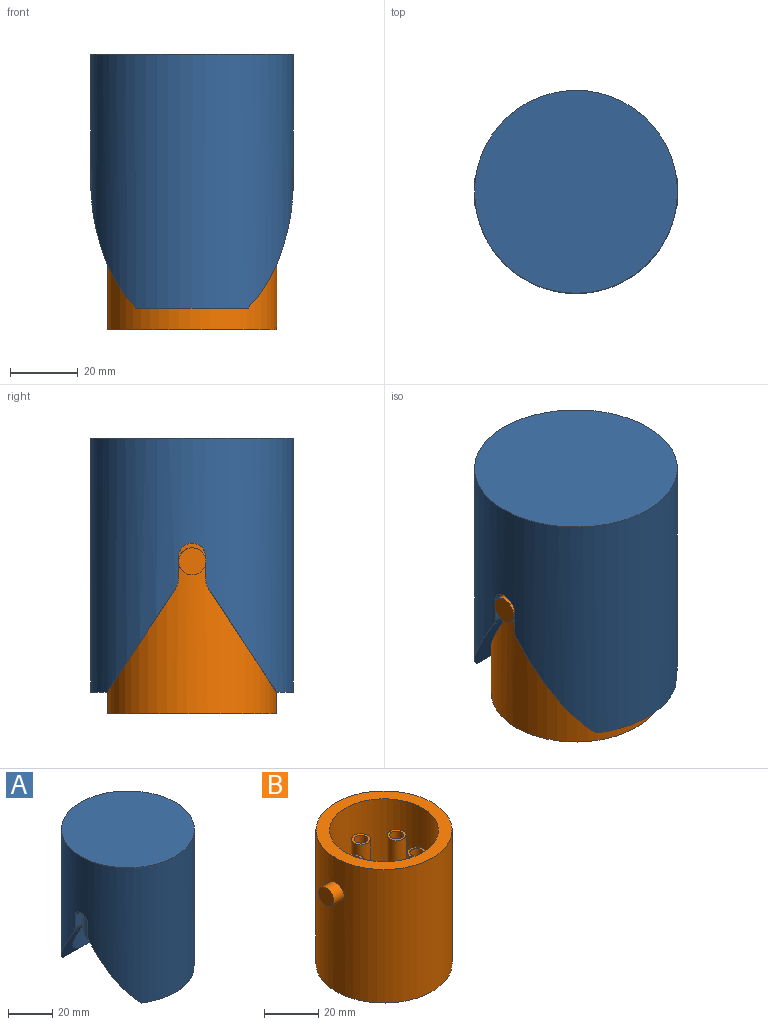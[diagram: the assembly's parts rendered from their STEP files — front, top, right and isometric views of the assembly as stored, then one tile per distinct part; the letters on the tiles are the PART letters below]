
ASSEMBLY  parts=2 mates=1
PART A: 42 faces, bbox 60x60x75 mm
  f0: cylinder r=25mm len=70mm, axis (0,0,1), area 8690.1mm2, adj f4,f28,f29,f30,f31,f32,f33,f34
  f1: cylinder r=30mm len=75mm, axis (0,0,-1), area 11956.4mm2, adj f2,f3,f27,f28,f29,f30,f31,f32
  f2: plane 33.17x5mm, normal (0,0,-1), area 112.5mm2, adj f1,f29,f36
  f3: plane 33.17x5mm, normal (0,0,-1), area 112.5mm2, adj f1,f30,f37
  f4: plane 50x50mm, normal (0,0,-1), area 706.9mm2, adj f0,f12
  f5: cylinder r=2.5mm len=20mm, axis (0,0,-1), area 314.2mm2, adj f6,f16
  f6: plane 5x5mm, normal (0,0,-1), area 19.6mm2, adj f5
  f7: cylinder r=3.5mm len=20mm, axis (0,0,-1), area 439.8mm2, adj f13,f18
  f8: cylinder r=3.5mm len=20mm, axis (0,0,-1), area 439.8mm2, adj f13,f17
  f9: cylinder r=3.5mm len=20mm, axis (0,0,-1), area 439.8mm2, adj f13,f16
  f10: cylinder r=3.5mm len=20mm, axis (0,0,-1), area 439.8mm2, adj f13,f15
  f11: cylinder r=3.5mm len=20mm, axis (0,0,-1), area 439.8mm2, adj f13,f14
  f12: cylinder r=20mm len=50mm, axis (0,0,-1), area 6283.2mm2, adj f4,f13
  f13: plane 40x40mm, normal (0,0,-1), area 1064.2mm2, adj f7,f8,f9,f10,f11,f12
  f14: plane 7x7mm, normal (0,0,-1), area 18.8mm2, adj f11,f25
  f15: plane 7x7mm, normal (0,0,-1), area 18.8mm2, adj f10,f21
  f16: plane 7x7mm, normal (0,0,-1), area 18.8mm2, adj f5,f9
  f17: plane 7x7mm, normal (0,0,-1), area 18.8mm2, adj f8,f23
  f18: plane 7x7mm, normal (0,0,-1), area 18.8mm2, adj f7,f19
  f19: cylinder r=2.5mm len=20mm, axis (0,0,-1), area 314.2mm2, adj f18,f20
  f20: plane 5x5mm, normal (0,0,-1), area 19.6mm2, adj f19
  f21: cylinder r=2.5mm len=20mm, axis (0,0,-1), area 314.2mm2, adj f15,f22
  f22: plane 5x5mm, normal (0,0,-1), area 19.6mm2, adj f21
  f23: cylinder r=2.5mm len=20mm, axis (0,0,-1), area 314.2mm2, adj f17,f24
  f24: plane 5x5mm, normal (0,0,-1), area 19.6mm2, adj f23
  f25: cylinder r=2.5mm len=20mm, axis (0,0,-1), area 314.2mm2, adj f14,f26
  f26: plane 5x5mm, normal (0,0,-1), area 19.6mm2, adj f25
  f27: plane 60x60mm, normal (0,0,1), area 2827.4mm2, adj f1
  f28: cylinder r=5mm len=5.2mm, axis (1,0,0), area 14.7mm2, adj f0,f1,f29,f34
  f29: plane 30.75x29.61mm, normal (0,0.84,-0.55), area 246.9mm2, adj f0,f1,f2,f28
  f30: plane 30.75x29.61mm, normal (0,-0.84,-0.55), area 246.9mm2, adj f0,f1,f3,f31
  f31: cylinder r=5mm len=5.2mm, axis (1,0,0), area 14.7mm2, adj f0,f1,f30,f32
  f32: plane 6.51x5.05mm, normal (0,-1,0), area 32.9mm2, adj f0,f1,f31,f33
  f33: cylinder r=4mm len=8mm, axis (1,0,0), area 63.2mm2, adj f0,f1,f32,f34
  f34: plane 6.51x5.05mm, normal (0,1,0), area 32.9mm2, adj f0,f1,f28,f33
  f35: cylinder r=5mm len=5.2mm, axis (-1,0,0), area 14.7mm2, adj f0,f1,f36,f41
  f36: plane 30.75x29.61mm, normal (0,0.84,-0.55), area 246.9mm2, adj f0,f1,f2,f35
  f37: plane 30.75x29.61mm, normal (0,-0.84,-0.55), area 246.9mm2, adj f0,f1,f3,f38
  f38: cylinder r=5mm len=5.2mm, axis (-1,0,0), area 14.7mm2, adj f0,f1,f37,f39
  f39: plane 6.51x5.05mm, normal (0,-1,0), area 32.9mm2, adj f0,f1,f38,f40
  f40: cylinder r=4mm len=8mm, axis (-1,0,0), area 63.2mm2, adj f0,f1,f39,f41
  f41: plane 6.51x5.05mm, normal (0,1,0), area 32.9mm2, adj f0,f1,f35,f40
PART B: 29 faces, bbox 60x50x60 mm
  f0: cylinder r=20mm len=40mm, axis (0,0,-1), area 4398.2mm2, adj f2,f3
  f1: cylinder r=25mm len=60mm, axis (0,0,-1), area 9324mm2, adj f2,f4,f25,f27
  f2: plane 50x50mm, normal (0,0,1), area 706.9mm2, adj f0,f1
  f3: plane 40x40mm, normal (0,0,1), area 1064.2mm2, adj f0,f6,f10,f14,f18,f22
  f4: plane 50x50mm, normal (0,0,-1), area 1963.5mm2, adj f1
  f5: cylinder r=2.5mm len=25mm, axis (0,0,-1), area 392.7mm2, adj f7,f8
  f6: cylinder r=3.5mm len=25mm, axis (0,0,-1), area 549.8mm2, adj f3,f7
  f7: plane 7x7mm, normal (0,0,1), area 18.8mm2, adj f5,f6
  f8: plane 5x5mm, normal (0,0,1), area 19.6mm2, adj f5
  f9: cylinder r=2.5mm len=25mm, axis (0,0,-1), area 392.7mm2, adj f11,f12
  f10: cylinder r=3.5mm len=25mm, axis (0,0,-1), area 549.8mm2, adj f3,f11
  f11: plane 7x7mm, normal (0,0,1), area 18.8mm2, adj f9,f10
  f12: plane 5x5mm, normal (0,0,1), area 19.6mm2, adj f9
  f13: cylinder r=2.5mm len=25mm, axis (0,0,-1), area 392.7mm2, adj f15,f16
  f14: cylinder r=3.5mm len=25mm, axis (0,0,-1), area 549.8mm2, adj f3,f15
  f15: plane 7x7mm, normal (0,0,1), area 18.8mm2, adj f13,f14
  f16: plane 5x5mm, normal (0,0,1), area 19.6mm2, adj f13
  f17: cylinder r=2.5mm len=25mm, axis (0,0,-1), area 392.7mm2, adj f19,f20
  f18: cylinder r=3.5mm len=25mm, axis (0,0,-1), area 549.8mm2, adj f3,f19
  f19: plane 7x7mm, normal (0,0,1), area 18.8mm2, adj f17,f18
  f20: plane 5x5mm, normal (0,0,1), area 19.6mm2, adj f17
  f21: cylinder r=2.5mm len=25mm, axis (0,0,-1), area 392.7mm2, adj f23,f24
  f22: cylinder r=3.5mm len=25mm, axis (0,0,-1), area 549.8mm2, adj f3,f23
  f23: plane 7x7mm, normal (0,0,1), area 18.8mm2, adj f21,f22
  f24: plane 5x5mm, normal (0,0,1), area 19.6mm2, adj f21
  f25: cylinder r=4mm len=8mm, axis (1,0,0), area 129.7mm2, adj f1,f26
  f26: plane 8x8mm, normal (-1,0,0), area 50.3mm2, adj f25
  f27: cylinder r=4mm len=8mm, axis (-1,0,0), area 129.7mm2, adj f1,f28
  f28: plane 8x8mm, normal (1,0,0), area 50.3mm2, adj f27
PLACE A t=(0,0,-55)mm
PLACE B rot(axis=(0,0,1),0.1deg) t=(0,0,-56.38)mm
MATE cylindrical B.f0 <-> A.f0  axis (0,0,-1) through (0,0,-51.38)mm
